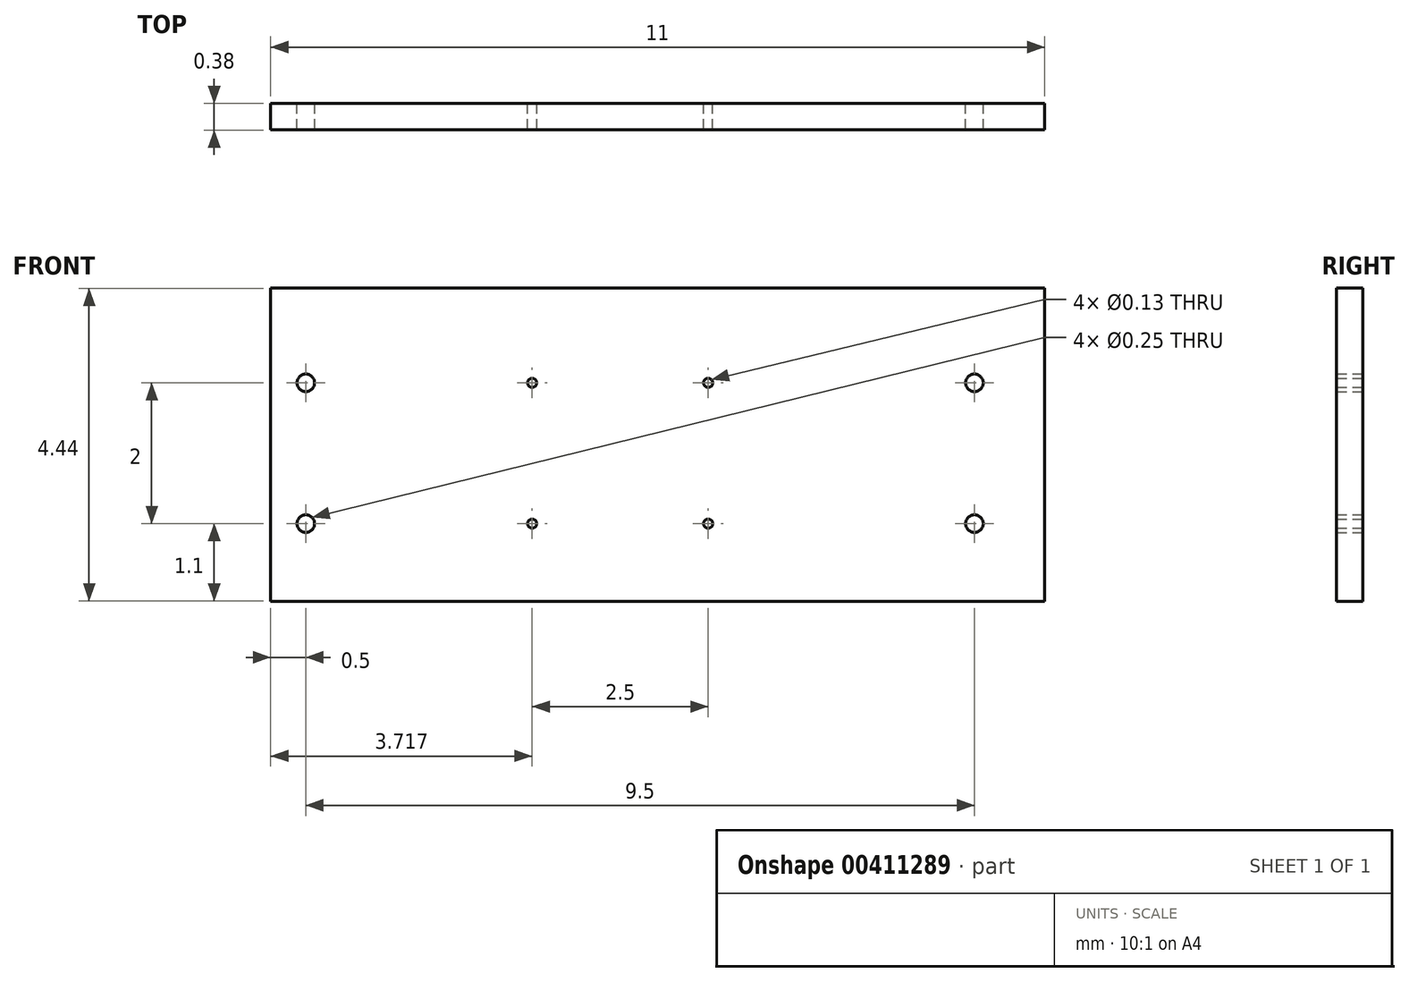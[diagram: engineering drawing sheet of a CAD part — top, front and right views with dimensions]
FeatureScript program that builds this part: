
annotation { "Feature Type Name" : "Feature", "Feature Type Description" : "" }
export const myFeature = defineFeature(function(context is Context, id is Id, definition is map)
    precondition{}
    {
        {
            var Q0;
            Q0=qCreatedBy(makeId("Front.planeOp"),FACE);
            var sketch = newSketch(context, id + "F0", { "sketchPlane" : qUnion([Q0])});
            skLineSegment(sketch, "E0.bottom", {"start": v(-6, 2.34) * mm, "end": v(5, 2.34) * mm});
            skLineSegment(sketch, "E0.top", {"start": v(-6, -2.1) * mm, "end": v(5, -2.1) * mm});
            skLineSegment(sketch, "E0.left", {"start": v(-6, 2.34) * mm, "end": v(-6, -2.1) * mm});
            skLineSegment(sketch, "E0.right", {"start": v(5, 2.34) * mm, "end": v(5, -2.1) * mm});
            skLineSegment(sketch, "E1", {"start": v(-5.99, 0) * mm, "end": v(6, 0) * mm, "construction": true});
            skLineSegment(sketch, "E2", {"start": v(0, 3.6) * mm, "end": v(0, -3.6) * mm});
            skLineSegment(sketch, "E3.0", {"start": v(-5.99, 1) * mm, "end": v(6, 1) * mm, "construction": true});
            skLineSegment(sketch, "E4.0", {"start": v(-5.99, -1) * mm, "end": v(6, -1) * mm, "construction": true});
            skLineSegment(sketch, "E5.0", {"start": v(-2.28, 1.06) * mm, "end": v(-2.28, -1.06) * mm, "construction": true});
            skLineSegment(sketch, "E6.0", {"start": v(0.22, 1.06) * mm, "end": v(0.22, -1.06) * mm, "construction": true});
            skLineSegment(sketch, "E7.0", {"start": v(4, 1.13) * mm, "end": v(4, -1.13) * mm, "construction": true});
            skLineSegment(sketch, "E8.0", {"start": v(-5.5, 1.13) * mm, "end": v(-5.5, -1.13) * mm, "construction": true});
            skCircle(sketch, "E9", {"center": v(-5.5, 1) * mm, "radius": 0.12 * mm});
            skCircle(sketch, "E10", {"center": v(-2.28, 1) * mm, "radius": 0.07 * mm});
            skCircle(sketch, "E11", {"center": v(0.22, 1) * mm, "radius": 0.07 * mm});
            skCircle(sketch, "E12", {"center": v(4, 1) * mm, "radius": 0.12 * mm});
            skCircle(sketch, "E13.MirrorC", {"center": v(-5.5, -1) * mm, "radius": 0.12 * mm});
            skCircle(sketch, "E14.MirrorC", {"center": v(-2.28, -1) * mm, "radius": 0.07 * mm});
            skCircle(sketch, "E15.MirrorC", {"center": v(0.22, -1) * mm, "radius": 0.07 * mm});
            skCircle(sketch, "E16.MirrorC", {"center": v(4, -1) * mm, "radius": 0.12 * mm});
            skSolve(sketch);
        }
        {
            var Q0;
            Q0 = qSketchRegion(id + "F0", true);
            extrude(context, id + "F1", {"entities" : qUnion([Q0]), "depth" : 0.38 * mm});
        }
    });
